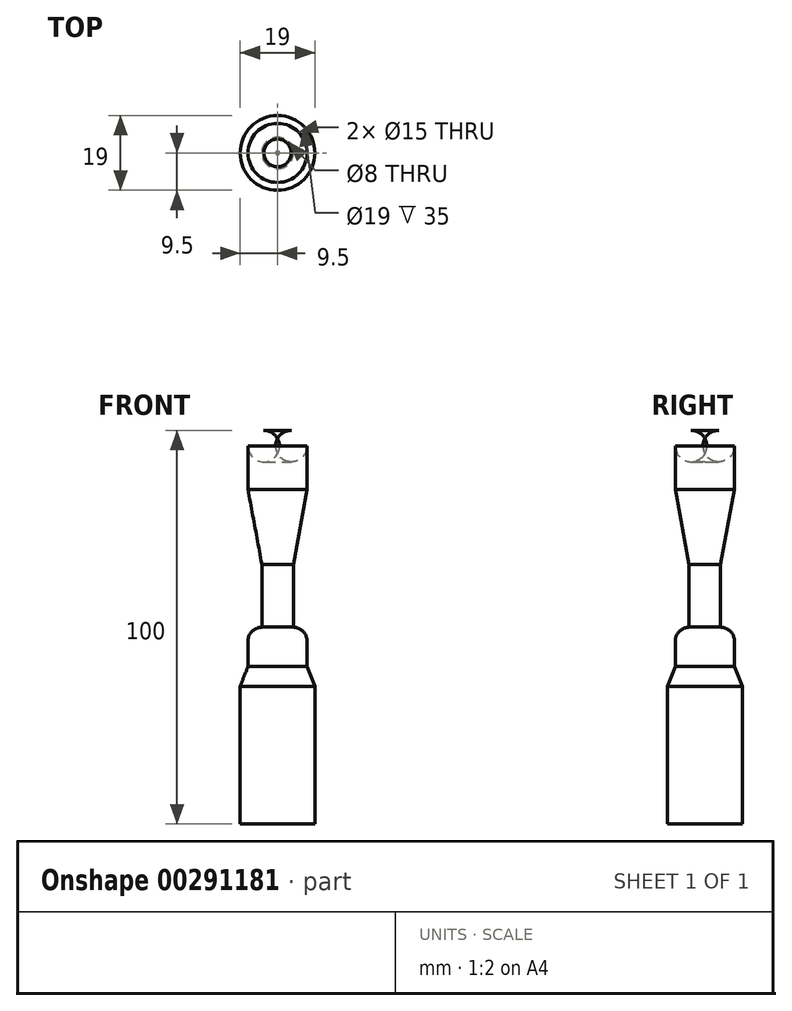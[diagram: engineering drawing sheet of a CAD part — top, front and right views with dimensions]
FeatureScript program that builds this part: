
annotation { "Feature Type Name" : "Feature", "Feature Type Description" : "" }
export const myFeature = defineFeature(function(context is Context, id is Id, definition is map)
    precondition{}
    {
        {
            var Q0;
            Q0=qCreatedBy(makeId("Front.planeOp"),FACE);
            var sketch = newSketch(context, id + "F0", { "sketchPlane" : qUnion([Q0])});
            skLineSegment(sketch, "E0", {"start": v(0, 0) * mm, "end": v(3.5, 0) * mm});
            skArc(sketch, "E1", {"start": v(7.5, -4) * mm, "mid": v(6.33, -1.17) * mm, "end": v(3.5, 0) * mm});
            skLineSegment(sketch, "E2", {"start": v(7.5, -4) * mm, "end": v(7.5, -15) * mm});
            skLineSegment(sketch, "E3", {"start": v(7.5, -15) * mm, "end": v(4, -34) * mm});
            skLineSegment(sketch, "E4", {"start": v(0, 0) * mm, "end": v(0, -100) * mm, "construction": true});
            skLineSegment(sketch, "E5", {"start": v(4, -34) * mm, "end": v(4, -50) * mm});
            skArc(sketch, "E6", {"start": v(7.5, -53.5) * mm, "mid": v(6.47, -51.03) * mm, "end": v(4, -50) * mm});
            skLineSegment(sketch, "E7", {"start": v(7.5, -53.5) * mm, "end": v(7.5, -60) * mm});
            skLineSegment(sketch, "E8", {"start": v(7.5, -60) * mm, "end": v(9.5, -65) * mm});
            skLineSegment(sketch, "E9", {"start": v(9.5, -65) * mm, "end": v(9.5, -100) * mm});
            skLineSegment(sketch, "E10", {"start": v(9.5, -100) * mm, "end": v(0, -100) * mm});
            skSolve(sketch);
        }
        {
            var Q0;
            Q0=sQuery(id+"F0.wireOp",EDGE,"E6");
            var Q1;
            Q1=sQuery(id+"F0.wireOp",EDGE,"E7");
            var Q2;
            Q2=sQuery(id+"F0.wireOp",EDGE,"E3");
            var Q3;
            Q3=sQuery(id+"F0.wireOp",EDGE,"E5");
            var Q4;
            Q4=sQuery(id+"F0.wireOp",EDGE,"E9");
            var Q5;
            Q5=sQuery(id+"F0.wireOp",EDGE,"E10");
            var Q6;
            Q6=sQuery(id+"F0.wireOp",EDGE,"E2");
            var Q7;
            Q7=sQuery(id+"F0.wireOp",EDGE,"E1");
            var Q8;
            Q8=sQuery(id+"F0.wireOp",EDGE,"E8");
            var Q9;
            Q9=sQuery(id+"F0.wireOp",EDGE,"E0");
            var Q10;
            Q10=sQuery(id+"F0.wireOp",EDGE,"E4");
            revolve(context, id + "F1", {"bodyType" : ToolBodyType.SURFACE, "surfaceEntities" : qUnion([Q0, Q1, Q2, Q3, Q4, Q5, Q6, Q7, Q8, Q9]), "axis" : qUnion([Q10]), "revolveType" : RevolveType.FULL});
        }
    });
